FREECAD ASSEMBLY — COMPONENT RECIPES ("1.1deltabot_assembly")

This assembly document has 19 components, labeled P0..P18 below (a component is one placed body or linked part). 10 of them carry a construction recipe — the FreeCAD feature program that regenerates the part from scratch, quoted from this document or its linked companion documents; the rest are supplied as boundary geometry only. No exploded tour is included for this assembly.
COMPONENT P0 — geometry summary ("motorb"; no construction recipe available for this part):
  bounding box: 75.4 x 57.0 x 56.7 mm
  tessellated surface: 25,604 triangles
  volume: 98013 mm^3 (40% of its bounding box)
COMPONENT P1 — geometry summary ("motorc"; no construction recipe available for this part):
  bounding box: 79.7 x 76.4 x 56.8 mm
  tessellated surface: 25,604 triangles
  volume: 98013 mm^3 (28% of its bounding box)
COMPONENT P2 — geometry summary ("SI8T/K Rod End Bearing v003"; no construction recipe available for this part):
  bounding box: 49.0 x 32.7 x 24.1 mm
  tessellated surface: 22,464 triangles
  volume: 6438 mm^3 (17% of its bounding box)
COMPONENT P3 — geometry summary ("SI8T/K Rod End Bearing v004"; no construction recipe available for this part):
  bounding box: 45.7 x 35.5 x 30.6 mm
  tessellated surface: 22,464 triangles
  volume: 6438 mm^3 (13% of its bounding box)
COMPONENT P4 — geometry summary ("SI8T/K Rod End Bearing v005"; no construction recipe available for this part):
  bounding box: 45.7 x 35.5 x 30.6 mm
  tessellated surface: 22,464 triangles
  volume: 6438 mm^3 (13% of its bounding box)
COMPONENT P5 — geometry summary ("SI8T/K Rod End Bearing v006"; no construction recipe available for this part):
  bounding box: 48.3 x 35.5 x 14.1 mm
  tessellated surface: 22,464 triangles
  volume: 6438 mm^3 (27% of its bounding box)
COMPONENT P6 — geometry summary ("SI8T/K Rod End Bearing v007"; no construction recipe available for this part):
  bounding box: 48.3 x 35.5 x 14.1 mm
  tessellated surface: 22,464 triangles
  volume: 6438 mm^3 (27% of its bounding box)
COMPONENT P7 — geometry summary ("SI8T/K Rod End Bearing v2"; no construction recipe available for this part):
  bounding box: 49.0 x 32.7 x 24.1 mm
  tessellated surface: 22,464 triangles
  volume: 6438 mm^3 (17% of its bounding box)
COMPONENT P8 — recipe-attached ("base", a linked part whose construction recipe lives in a companion FreeCAD document of the same project; that document's serialized recipe follows).
Construction recipe (the companion document, serialized — sketch geometry with constraints, then the solid features built on it; lengths are millimeters unless a unit is written):

FCSTD DOCUMENT  (FreeCAD 1.0R38641 +468 (Git))
Label: main
License: All rights reserved
LicenseURL: https://en.wikipedia.org/wiki/All_rights_reserved
objects: Sketcher::SketchObject×17, PartDesign::Pad×10, PartDesign::Body×7, PartDesign::Plane×6, PartDesign::Pocket×4, App::Part×4, PartDesign::ShapeBinder×2, PartDesign::Chamfer×2, Spreadsheet::Sheet×1, PartDesign::AdditiveLoft×1, PartDesign::Fillet×1, PartDesign::SubtractiveBox×1, PartDesign::PolarPattern×1
note: 108 computed .brp shape members not serialized (recipe doc carries the construction recipe); baked Part::Feature solids carry a one-line shape summary decoded from their .brp

FEATURE [Spreadsheet::Sheet] Spreadsheet  label="ss"
  cells = A1='deltabot calculation - values for kinetic | https://www.marginallyclever.com/other/samples/fk-ik-test.html; A3='Base radius (f); B3(f)=300; D3='vslot_length; E3(vslot_length)==<<main>>#<<base_triangle_sketch>>.Constraints.vslot_length; A4='Bicep length (rf); B4(rf)=200; C4='!= tube actual length; A5='Bicep inerdia (od_rf); B5(od_rf)=30; A6='Bicep outerdia (id_rf); B6(id_rf)=27.95; A7='Bicep end length (end_rf); B7(end_rf)=25; A11='Forearm length (re); B11(re)=300; A12='End Effector radius (e); A13='Base to floor distance (b)
FEATURE [Sketcher::SketchObject] Sketch
  ArcFitTolerance = 0
  AttachmentSupport = -> [XY_Plane]
  FullyConstrained = true
  MakeInternals = false
  MapMode = 5
  sketch-geometry (1):
    g0: Circle CenterX=0 CenterY=0 CenterZ=0 NormalX=0 NormalY=0 NormalZ=1 AngleXU=0 Radius=4
  constraints (2):
    c: Coincident(g0,g-1)
    c: Diameter(g0) = 8
FEATURE [PartDesign::Pad] Pad
  Direction = (0,0,1)
  Length = 300
  Length2 = 10
  Midplane = true
  Profile = -> Sketch
  ReferenceAxis = -> Sketch [N_Axis]
  Suppressed = false
  Type = 0
  expr: Length = Spreadsheet.re
FEATURE [Sketcher::SketchObject] Sketch001
  ArcFitTolerance = 0
  AttachmentSupport = -> [XY_Plane001]
  FullyConstrained = true
  MakeInternals = false
  MapMode = 5
  expr: Constraints[1] = Spreadsheet.od_rf
  expr: Constraints[3] = <<ss>>.id_rf
  sketch-geometry (2):
    g0: Circle CenterX=0 CenterY=0 CenterZ=0 NormalX=0 NormalY=0 NormalZ=1 AngleXU=0 Radius=15
    g1: Circle CenterX=0 CenterY=0 CenterZ=0 NormalX=0 NormalY=0 NormalZ=1 AngleXU=0 Radius=13.975
  constraints (4):
    c: Coincident(g0,g-1)
    c: Diameter(g0) = 30
    c: Coincident(g1,g0)
    c: Diameter(g1) = 27.95
FEATURE [PartDesign::Pad] Pad001
  Direction = (0,0,1)
  Length = 146
  Length2 = 10
  Midplane = true
  Profile = -> Sketch001
  ReferenceAxis = -> Sketch001 [N_Axis]
  Suppressed = false
  Type = 0
  expr: Length = <<ss>>.rf - <<ss>>.end_rf - 29
FEATURE [PartDesign::Body] Body001  label="tube_bicep"
  AllowCompound = false
  Group = -> [Sketch001,Pad001]
  Origin = -> Origin001
  Tip = -> Pad001
FEATURE [PartDesign::ShapeBinder] ReferencePad001
  Placement = pos=(0,0,73) rot=(0,0,1;0rad)
  Support = -> [Pad001]
  TraceSupport = false
FEATURE [PartDesign::Plane] DatumPlane
  AttachmentSupport = -> [ReferencePad001]
  Length = 61.3058
  MapMode = 5
  Placement = pos=(0,0,73) rot=(0,0,1;0rad)
  ResizeMode = 0
  Width = 75.2168
FEATURE [Sketcher::SketchObject] Sketch002
  ArcFitTolerance = 0
  AttachmentSupport = -> [DatumPlane]
  FullyConstrained = true
  MakeInternals = false
  MapMode = 5
  Placement = pos=(0,0,73) rot=(0,0,1;0rad)
  expr: Constraints[1] = <<ss>>.id_rf
  sketch-geometry (1):
    g0: Circle CenterX=0 CenterY=0 CenterZ=0 NormalX=0 NormalY=0 NormalZ=1 AngleXU=0 Radius=13.975
  constraints (2):
    c: Coincident(g0,g-1)
    c: Diameter(g0) = 27.95
FEATURE [PartDesign::Pad] Pad002
  Direction = (0,0,1)
  Length = 15
  Length2 = 10
  Placement = pos=(0,0,73) rot=(0,0,1;0rad)
  Profile = -> Sketch002
  ReferenceAxis = -> Sketch002 [N_Axis]
  Reversed = true
  Suppressed = false
  Type = 0
FEATURE [Sketcher::SketchObject] Sketch003
  ArcFitTolerance = 0
  AttachmentSupport = -> [DatumPlane]
  FullyConstrained = true
  MakeInternals = false
  MapMode = 5
  Placement = pos=(0,0,73) rot=(0,0,1;0rad)
  expr: Constraints[1] = <<ss>>.od_rf
  sketch-geometry (1):
    g0: Circle CenterX=0 CenterY=0 CenterZ=0 NormalX=0 NormalY=0 NormalZ=1 AngleXU=0 Radius=15
  constraints (2):
    c: Coincident(g0,g-1)
    c: Diameter(g0) = 30
FEATURE [PartDesign::Pad] Pad003
  BaseFeature = -> Pad002
  Direction = (0,0,1)
  Length = 25
  Length2 = 10
  Placement = pos=(0,0,73) rot=(0,0,1;0rad)
  Profile = -> Sketch003
  ReferenceAxis = -> Sketch003 [N_Axis]
  Suppressed = false
  Type = 0
  expr: Length = <<ss>>.end_rf
FEATURE [PartDesign::Plane] DatumPlane001
  AttachmentOffset = pos=(0,0,0) rot=(0,1,0;1.5708rad)
  AttachmentSupport = -> [Pad003]
  Length = 138.272
  MapMode = 45
  Placement = pos=(-1.8e-15,1e-16,85.5) rot=(0,1,0;1.5708rad)
  ResizeMode = 0
  Width = 81.4772
FEATURE [Sketcher::SketchObject] Sketch004
  ArcFitTolerance = 0
  AttachmentSupport = -> [DatumPlane001]
  ExternalGeometry = -> [Pad003]
  FullyConstrained = false
  MakeInternals = false
  MapMode = 5
  Placement = pos=(-1.8e-15,1e-16,85.5) rot=(0,1,0;1.5708rad)
  sketch-geometry (6):
    g0: Circle CenterX=0 CenterY=-22.7402 CenterZ=0 NormalX=0 NormalY=0 NormalZ=1 AngleXU=0 Radius=3
    g1: ArcOfCircle CenterX=0 CenterY=-22.7402 CenterZ=0 NormalX=0 NormalY=0 NormalZ=1 AngleXU=0 Radius=7.5 StartAngle=2.63197 EndAngle=6.07379
    g2: LineSegment StartX=-6.54695 StartY=-19.0813 StartZ=0 EndX=4.11697 EndY=0 EndZ=0
    g3: LineSegment StartX=4.11697 StartY=0 StartZ=0 EndX=12.5 EndY=0 EndZ=0
    g4: LineSegment StartX=7.33618 StartY=-24.2992 StartZ=0 EndX=12.5 EndY=0 EndZ=0
    g5: LineSegment [constr] StartX=12.5 StartY=15 StartZ=0 EndX=-6.54695 EndY=-19.0813 EndZ=0
  constraints (14):
    c: PointOnObject(g0,g-2)
    c: Diameter(g0) = 6
    c: Coincident(g1,g0)
    c: Diameter(g1) = 15
    c: Tangent(g1,g2) = 1.5708
    c: Coincident(g2,g3)
    c: Horizontal(g3)
    c: PointOnObject(g2,g-1)
    c: Tangent(g1,g4) = -1.5708
    c: Coincident(g4,g3)
    c: PointOnObject(g3,g-5)
    c: Coincident(g5,g-4)
    c: Coincident(g5,g1)
    c: PointOnObject(g2,g5)
FEATURE [PartDesign::Pad] Pad004
  BaseFeature = -> Pad003
  Direction = (1,0,2e-16)
  Length = 30
  Length2 = 10
  Midplane = true
  Placement = pos=(0,0,73) rot=(0,0,1;0rad)
  Profile = -> Sketch004
  ReferenceAxis = -> Sketch004 [N_Axis]
  Suppressed = false
  Type = 0
  expr: Length = <<ss>>.od_rf
FEATURE [PartDesign::ShapeBinder] ReferencePad002
  Placement = pos=(0,0,-73) rot=(0,0,1;0rad)
  Support = -> [Pad001]
  TraceSupport = false
FEATURE [PartDesign::Plane] DatumPlane002
  AttachmentSupport = -> [ReferencePad002]
  Length = 60
  MapMode = 5
  Placement = pos=(0,0,-73) rot=(1,0,0;3.14159rad)
  ResizeMode = 0
  Width = 60
FEATURE [Sketcher::SketchObject] Sketch005
  ArcFitTolerance = 0
  AttachmentSupport = -> [DatumPlane002]
  FullyConstrained = true
  MakeInternals = false
  MapMode = 5
  Placement = pos=(0,0,-73) rot=(1,0,0;3.14159rad)
  expr: Constraints[1] = <<ss>>.id_rf
  sketch-geometry (1):
    g0: Circle CenterX=0 CenterY=0 CenterZ=0 NormalX=0 NormalY=0 NormalZ=1 AngleXU=0 Radius=13.975
  constraints (2):
    c: Coincident(g0,g-1)
    c: Diameter(g0) = 27.95
FEATURE [PartDesign::Pad] Pad005
  Direction = (0,0,-1)
  Length = 15
  Length2 = 10
  Placement = pos=(0,0,-73) rot=(1,0,0;3.14159rad)
  Profile = -> Sketch005
  ReferenceAxis = -> Sketch005 [N_Axis]
  Reversed = true
  Suppressed = false
  Type = 0
FEATURE [Sketcher::SketchObject] Sketch006
  ArcFitTolerance = 0
  AttachmentSupport = -> [DatumPlane002]
  FullyConstrained = true
  MakeInternals = false
  MapMode = 5
  Placement = pos=(0,0,-73) rot=(1,0,0;3.14159rad)
  expr: Constraints[1] = <<ss>>.od_rf
  sketch-geometry (1):
    g0: Circle CenterX=0 CenterY=0 CenterZ=0 NormalX=0 NormalY=0 NormalZ=1 AngleXU=0 Radius=15
  constraints (2):
    c: Coincident(g0,g-1)
    c: Diameter(g0) = 30
FEATURE [PartDesign::Plane] DatumPlane003
  AttachmentOffset = pos=(0,0,20) rot=(0,0,1;0rad)
  AttachmentSupport = -> [DatumPlane002]
  Length = 60
  MapMode = 5
  Placement = pos=(0,0,-93) rot=(1,0,0;3.14159rad)
  ResizeMode = 0
  Width = 60
FEATURE [Sketcher::SketchObject] Sketch007
  ArcFitTolerance = 0
  AttachmentSupport = -> [DatumPlane003]
  FullyConstrained = true
  MakeInternals = false
  MapMode = 5
  Placement = pos=(0,0,-93) rot=(1,0,0;3.14159rad)
  expr: Constraints[10] = <<ss>>.od_rf
  expr: Constraints[11] = <<ss>>.od_rf
  sketch-geometry (5):
    g0: LineSegment StartX=-15 StartY=-15 StartZ=0 EndX=-15 EndY=15 EndZ=0
    g1: LineSegment StartX=-15 StartY=15 StartZ=0 EndX=15 EndY=15 EndZ=0
    g2: LineSegment StartX=15 StartY=15 StartZ=0 EndX=15 EndY=-15 EndZ=0
    g3: LineSegment StartX=15 StartY=-15 StartZ=0 EndX=-15 EndY=-15 EndZ=0
    g4: GeomPoint [constr] X=0 Y=0 Z=0
  constraints (12):
    c: Coincident(g0,g1)
    c: Coincident(g1,g2)
    c: Coincident(g2,g3)
    c: Coincident(g3,g0)
    c: Horizontal(g1)
    c: Horizontal(g3)
    c: Vertical(g0)
    c: Vertical(g2)
    c: Symmetric(g1,g0,g4)
    c: Coincident(g4,g-1)
    c: DistanceX(g1,g1) = 30
    c: DistanceY(g2,g2) = 30
FEATURE [PartDesign::AdditiveLoft] AdditiveLoft
  BaseFeature = -> Pad005
  Closed = false
  Placement = pos=(0,0,-73) rot=(1,0,0;3.14159rad)
  Profile = -> Sketch006
  Ruled = false
  Sections = -> [Sketch007]
  Suppressed = false
FEATURE [PartDesign::Pad] Pad006
  BaseFeature = -> AdditiveLoft
  Direction = (0,0,-1)
  Length = 15
  Length2 = 10
  Placement = pos=(0,0,-73) rot=(1,0,0;3.14159rad)
  Profile = -> Sketch007
  ReferenceAxis = -> Sketch007 [N_Axis]
  Suppressed = false
  Type = 0
  expr: Length = <<ss>>.od_rf * 0.5
FEATURE [PartDesign::Fillet] Fillet
  Base = -> Pad006 [Edge25,Edge23]
  BaseFeature = -> Pad006
  Placement = pos=(0,0,-73) rot=(1,0,0;3.14159rad)
  Radius = 13.5
  SupportTransform = false
  Suppressed = false
  UseAllEdges = false
  expr: Radius = <<ss>>.od_rf * 0.45
FEATURE [PartDesign::Chamfer] Chamfer
  Angle = 45
  Base = -> Fillet [Face1,Face9]
  BaseFeature = -> Fillet
  ChamferType = 0
  FlipDirection = false
  Placement = pos=(0,0,-73) rot=(1,0,0;3.14159rad)
  Size = 1
  Size2 = 1
  SupportTransform = false
  Suppressed = false
  UseAllEdges = false
FEATURE [Sketcher::SketchObject] Sketch008
  ArcFitTolerance = 0
  AttachmentSupport = -> [Chamfer]
  ExternalGeometry = -> [Chamfer]
  FullyConstrained = true
  MakeInternals = false
  MapMode = 5
  Placement = pos=(15,0,-73) rot=(0.57735,-0.57735,0.57735;4.18879rad)
  expr: Constraints[7] = 7.5 / 2 - 0.1
  sketch-geometry (3):
    g0: Circle [constr] CenterX=-1.8e-15 CenterY=21 CenterZ=0 NormalX=0 NormalY=0 NormalZ=1 AngleXU=0 Radius=4.05
    g1: ArcOfCircle CenterX=-1.8e-15 CenterY=21 CenterZ=0 NormalX=0 NormalY=0 NormalZ=1 AngleXU=0 Radius=4.05 StartAngle=2.01898 EndAngle=7.4058
    g2: LineSegment StartX=-1.75499 StartY=24.65 StartZ=0 EndX=1.75499 EndY=24.65 EndZ=0
  constraints (8):
    c: Diameter(g0) = 8.1
    c: PointOnObject(g1,g0)
    c: Coincident(g1,g0)
    c: Coincident(g0,g-4)
    c: Horizontal(g2)
    c: Coincident(g1,g2)
    c: Coincident(g1,g2)
    c: DistanceY(g0,g1) = 3.65
FEATURE [PartDesign::Pocket] Pocket
  BaseFeature = -> Chamfer
  Direction = (-1,0,0)
  Length = 5
  Length2 = 5
  Placement = pos=(0,0,-73) rot=(1,0,0;3.14159rad)
  Profile = -> Sketch008
  ReferenceAxis = -> Sketch008 [N_Axis]
  Suppressed = false
  Type = 1
FEATURE [PartDesign::SubtractiveBox] Box
  AttacherType = Attacher::AttachEngine3D
  AttachmentOffset = pos=(-23,-39,0) rot=(0,0,1;0rad)
  AttachmentSupport = -> [Pad004]
  BaseFeature = -> Pad004
  Height = 44
  Length = 44
  MapMode = 5
  Placement = pos=(-23,-30.4742,98.4141) rot=(-1,0,0;0.509626rad)
  Refine = true
  Suppressed = false
  Width = 61
FEATURE [App::Part] Part002  label="tool"
  Origin = -> Origin010
FEATURE [Sketcher::SketchObject] Sketch010
  ArcFitTolerance = 1e-06
  AttachmentSupport = -> [XY_Plane011]
  FullyConstrained = true
  MakeInternals = false
  MapMode = 5
FEATURE [PartDesign::Body] Body  label="forearm_axis"
  AllowCompound = false
  Group = -> [Sketch,Pad,Sketch010]
  Origin = -> Origin
  Tip = -> Pad
FEATURE [App::Part] Part001  label="forearm"
  Group = -> [Body]
  Origin = -> Origin009
FEATURE [Sketcher::SketchObject] Sketch011  label="base_triangle_sketch"
  ArcFitTolerance = 1e-06
  AttachmentSupport = -> [XY_Plane012]
  FullyConstrained = true
  MakeInternals = false
  MapMode = 5
  sketch-geometry (12):
    g0: Circle [constr] CenterX=0 CenterY=0 CenterZ=0 NormalX=0 NormalY=0 NormalZ=1 AngleXU=0 Radius=150
    g1: LineSegment StartX=0 StartY=35 StartZ=0 EndX=-30.3109 EndY=-17.5 EndZ=0
    g2: LineSegment StartX=-30.3109 StartY=-17.5 StartZ=0 EndX=30.3109 EndY=-17.5 EndZ=0
    g3: LineSegment StartX=30.3109 StartY=-17.5 StartZ=0 EndX=0 EndY=35 EndZ=0
    g4: Circle [constr] CenterX=0 CenterY=0 CenterZ=0 NormalX=0 NormalY=0 NormalZ=1 AngleXU=0 Radius=35
    g5: LineSegment StartX=0 StartY=75 StartZ=0 EndX=-64.9519 EndY=-37.5 EndZ=0
    g6: LineSegment StartX=-64.9519 StartY=-37.5 StartZ=0 EndX=64.9519 EndY=-37.5 EndZ=0
    g7: LineSegment StartX=64.9519 StartY=-37.5 StartZ=0 EndX=0 EndY=75 EndZ=0
    g8: Circle [constr] CenterX=0 CenterY=0 CenterZ=0 NormalX=0 NormalY=0 NormalZ=1 AngleXU=0 Radius=75
    g9: LineSegment [constr] StartX=0 StartY=35 StartZ=0 EndX=89.6433 EndY=-120.267 EndZ=0
    g10: LineSegment [constr] StartX=30.3109 StartY=-17.5 StartZ=0 EndX=-148.976 EndY=-17.5 EndZ=0
    g11: LineSegment [constr] StartX=-30.3109 StartY=-17.5 StartZ=0 EndX=59.3324 EndY=137.767 EndZ=0
  constraints (34):
    c: Diameter(g0) = 300
    c: Coincident(g0,g-1)
    c: Coincident(g1,g2)
    c: Coincident(g2,g3)
    c: Coincident(g3,g1)
    c: Equal(g1,g2)
    c: Equal(g1,g3)
    c: PointOnObject(g1,g4)
    c: PointOnObject(g2,g4)
    c: PointOnObject(g3,g4)
    c: Coincident(g4,g0)
    c: Coincident(g5,g6)
    c: Coincident(g6,g7)
    c: Coincident(g7,g5)
    c: Equal(g5,g6)
    c: Equal(g5,g7)
    c: PointOnObject(g5,g8)
    c: PointOnObject(g6,g8)
    c: PointOnObject(g7,g8)
    c: Coincident(g8,g0)
    c: PointOnObject(g1,g-2)
    c: PointOnObject(g5,g-2)
    c: Distance(g7,g3) = 20
    c: Coincident(g9,g1)
    c: PointOnObject(g9,g0)
    c: PointOnObject(g2,g9)
    c: Coincident(g10,g2)
    c: PointOnObject(g10,g0)
    c: Horizontal(g10)
    c: Coincident(g11,g1)
    c: PointOnObject(g3,g11)
    c: PointOnObject(g11,g0)
    c: Diameter(g8) = 150
    c: Distance(g9,g9) = 179.287  'vslot_length'
FEATURE [PartDesign::Pad] Pad007
  Direction = (0,0,1)
  Length = 10
  Length2 = 10
  Profile = -> Sketch011
  ReferenceAxis = -> Sketch011 [N_Axis]
  Refine = true
  Suppressed = false
  Type = 0
FEATURE [Sketcher::SketchObject] Sketch015
  ArcFitTolerance = 1e-06
  AttachmentSupport = -> [XY_Plane014]
  FullyConstrained = false
  MakeInternals = false
  MapMode = 5
  sketch-geometry (50):
    g0: ArcOfCircle CenterX=0 CenterY=0 CenterZ=0 NormalX=0 NormalY=0 NormalZ=1 AngleXU=0 Radius=2.5 StartAngle=3.14159 EndAngle=6.28319
    g1: LineSegment StartX=-10 StartY=-5.1 StartZ=0 EndX=-10 EndY=-8.5 EndZ=0
    g2: ArcOfCircle CenterX=-8.5 CenterY=-8.5 CenterZ=0 NormalX=0 NormalY=0 NormalZ=1 AngleXU=0 Radius=1.5 StartAngle=3.14159 EndAngle=4.71239
    g3: LineSegment StartX=-8.5 StartY=-10 StartZ=0 EndX=-5.1 EndY=-10 EndZ=0
    g4: LineSegment StartX=-5.1 StartY=-10 StartZ=0 EndX=-3.1 EndY=-8 EndZ=0
    g5: LineSegment StartX=-3.1 StartY=-8 StartZ=0 EndX=-5.3 EndY=-8 EndZ=0
    g6: LineSegment StartX=-5.3 StartY=-8 StartZ=0 EndX=-5.3 EndY=-6.57279 EndZ=0
    g7: LineSegment StartX=-5.3 StartY=-6.57279 StartZ=0 EndX=-2.72721 EndY=-4 EndZ=0
    g8: LineSegment StartX=-2.72721 StartY=-4 StartZ=0 EndX=2.72721 EndY=-4 EndZ=0
    g9: LineSegment StartX=2.72721 StartY=-4 StartZ=0 EndX=5.3 EndY=-6.57279 EndZ=0
    g10: LineSegment StartX=5.3 StartY=-6.57279 StartZ=0 EndX=5.3 EndY=-8 EndZ=0
    g11: LineSegment StartX=5.3 StartY=-8 StartZ=0 EndX=3.1 EndY=-8 EndZ=0
    g12: LineSegment StartX=3.1 StartY=-8 StartZ=0 EndX=5.1 EndY=-10 EndZ=0
    g13: LineSegment StartX=5.1 StartY=-10 StartZ=0 EndX=8.5 EndY=-10 EndZ=0
    g14: ArcOfCircle CenterX=8.5 CenterY=-8.5 CenterZ=0 NormalX=0 NormalY=0 NormalZ=1 AngleXU=0 Radius=1.5 StartAngle=4.71239 EndAngle=6.28319
    g15: LineSegment StartX=10 StartY=-8.5 StartZ=0 EndX=10 EndY=-5.1 EndZ=0
    g16: LineSegment StartX=10 StartY=-5.1 StartZ=0 EndX=8 EndY=-3.1 EndZ=0
    g17: LineSegment StartX=8 StartY=-3.1 StartZ=0 EndX=8 EndY=-5.3 EndZ=0
    g18: LineSegment StartX=8 StartY=-5.3 StartZ=0 EndX=6.57279 EndY=-5.3 EndZ=0
    g19: LineSegment StartX=6.57279 StartY=-5.3 StartZ=0 EndX=4 EndY=-2.72721 EndZ=0
    g20: LineSegment StartX=4 StartY=-2.72721 StartZ=0 EndX=4 EndY=2.72721 EndZ=0
    g21: LineSegment StartX=4 StartY=2.72721 StartZ=0 EndX=6.57279 EndY=5.3 EndZ=0
    g22: LineSegment StartX=6.57279 StartY=5.3 StartZ=0 EndX=8 EndY=5.3 EndZ=0
    g23: LineSegment StartX=8 StartY=5.3 StartZ=0 EndX=8 EndY=3.1 EndZ=0
    g24: LineSegment StartX=8 StartY=3.1 StartZ=0 EndX=10 EndY=5.1 EndZ=0
    g25: LineSegment StartX=10 StartY=5.1 StartZ=0 EndX=10 EndY=8.5 EndZ=0
    g26: ArcOfCircle CenterX=8.5 CenterY=8.5 CenterZ=0 NormalX=0 NormalY=0 NormalZ=1 AngleXU=0 Radius=1.5 StartAngle=0 EndAngle=1.5708
    g27: LineSegment StartX=8.5 StartY=10 StartZ=0 EndX=5.1 EndY=10 EndZ=0
    g28: LineSegment StartX=5.1 StartY=10 StartZ=0 EndX=3.1 EndY=8 EndZ=0
    g29: LineSegment StartX=3.1 StartY=8 StartZ=0 EndX=5.3 EndY=8 EndZ=0
    g30: LineSegment StartX=5.3 StartY=8 StartZ=0 EndX=5.3 EndY=6.57279 EndZ=0
    g31: LineSegment StartX=5.3 StartY=6.57279 StartZ=0 EndX=2.72721 EndY=4 EndZ=0
    g32: LineSegment StartX=2.72721 StartY=4 StartZ=0 EndX=-2.72721 EndY=4 EndZ=0
    g33: LineSegment StartX=-2.72721 StartY=4 StartZ=0 EndX=-5.3 EndY=6.57279 EndZ=0
    g34: LineSegment StartX=-5.3 StartY=6.57279 StartZ=0 EndX=-5.3 EndY=8 EndZ=0
    g35: LineSegment StartX=-5.3 StartY=8 StartZ=0 EndX=-3.1 EndY=8 EndZ=0
    g36: LineSegment StartX=-3.1 StartY=8 StartZ=0 EndX=-5.1 EndY=10 EndZ=0
    g37: LineSegment StartX=-5.1 StartY=10 StartZ=0 EndX=-8.5 EndY=10 EndZ=0
    g38: ArcOfCircle CenterX=-8.5 CenterY=8.5 CenterZ=0 NormalX=0 NormalY=0 NormalZ=1 AngleXU=0 Radius=1.5 StartAngle=1.5708 EndAngle=3.14159
    g39: LineSegment StartX=-10 StartY=8.5 StartZ=0 EndX=-10 EndY=5.1 EndZ=0
    g40: LineSegment StartX=-10 StartY=5.1 StartZ=0 EndX=-8 EndY=3.1 EndZ=0
    g41: LineSegment StartX=-8 StartY=3.1 StartZ=0 EndX=-8 EndY=5.3 EndZ=0
    g42: LineSegment StartX=-8 StartY=5.3 StartZ=0 EndX=-6.57279 EndY=5.3 EndZ=0
    g43: LineSegment StartX=-6.57279 StartY=5.3 StartZ=0 EndX=-4 EndY=2.72721 EndZ=0
    g44: LineSegment StartX=-4 StartY=2.72721 StartZ=0 EndX=-4 EndY=-2.72721 EndZ=0
    g45: LineSegment StartX=-4 StartY=-2.72721 StartZ=0 EndX=-6.57279 EndY=-5.3 EndZ=0
    g46: LineSegment StartX=-6.57279 StartY=-5.3 StartZ=0 EndX=-8 EndY=-5.3 EndZ=0
    g47: LineSegment StartX=-8 StartY=-5.3 StartZ=0 EndX=-8 EndY=-3.1 EndZ=0
    g48: LineSegment StartX=-8 StartY=-3.1 StartZ=0 EndX=-10 EndY=-5.1 EndZ=0
    g49: ArcOfCircle CenterX=0 CenterY=0 CenterZ=0 NormalX=0 NormalY=0 NormalZ=1 AngleXU=0 Radius=2.5 StartAngle=0 EndAngle=3.14159
FEATURE [Sketcher::SketchObject] Sketch012
  ArcFitTolerance = 1e-06
  AttachmentSupport = -> [XY_Plane012]
  ExternalGeometry = -> [Sketch011]
  FullyConstrained = true
  MakeInternals = false
  MapMode = 5
  sketch-geometry (4):
    g0: Circle CenterX=11.3157 CenterY=35.4006 CenterZ=0 NormalX=0 NormalY=0 NormalZ=1 AngleXU=0 Radius=2.5
    g1: LineSegment [constr] StartX=-30.3109 StartY=-17.5 StartZ=0 EndX=32.476 EndY=18.75 EndZ=0
    g2: LineSegment [constr] StartX=23.8157 StartY=13.75 StartZ=0 EndX=11.3157 EndY=35.4006 EndZ=0
    g3: Circle CenterX=36.3157 CenterY=-7.90064 CenterZ=0 NormalX=0 NormalY=0 NormalZ=1 AngleXU=0 Radius=2.5
  constraints (11):
    c: Perpendicular(g-3,g1)
    c: Coincident(g1,g-4)
    c: PointOnObject(g2,g1)
    c: Perpendicular(g1,g2)
    c: PointOnObject(g1,g-3)
    c: Distance(g2,g1) = 10
    c: Coincident(g0,g2)
    c: Symmetric(g0,g3,g2)
    c: Equal(g3,g0)
    c: Diameter(g0) = 5
    c: Distance(g0,g3) = 50
FEATURE [PartDesign::Pocket] Pocket003
  BaseFeature = -> Pad007
  Direction = (0,0,-1)
  Length = 5
  Length2 = 5
  Profile = -> Sketch012
  ReferenceAxis = -> Sketch012 [N_Axis]
  Refine = true
  Reversed = true
  Suppressed = false
  Type = 1
FEATURE [PartDesign::PolarPattern] PolarPattern
  Angle = 360
  Axis = -> Sketch012 [N_Axis]
  BaseFeature = -> Pocket003
  Mode = 0
  Occurrences = 3
  Offset = 120
  Originals = -> [Pocket003]
  Refine = true
  Suppressed = false
  TransformMode = 0
FEATURE [PartDesign::Body] Body004  label="base_triangle"
  AllowCompound = false
  Group = -> [Sketch011,Pad007,Sketch012,Pocket003,PolarPattern]
  Origin = -> Origin012
  Tip = -> PolarPattern
FEATURE [App::Part] Part003  label="base"
  Group = -> [Body004]
  Origin = -> Origin011
FEATURE [PartDesign::Pad] Pad008
  Direction = (0,0,1)
  Length = 179.287
  Length2 = 10
  Profile = -> Sketch015
  ReferenceAxis = -> Sketch015 [N_Axis]
  Refine = true
  Suppressed = false
  Type = 0
  expr: Length = <<ss>>.vslot_length
FEATURE [PartDesign::Body] Body006  label="vslot"
  AllowCompound = false
  Group = -> [Sketch015,Pad008]
  Origin = -> Origin024
  Tip = -> Pad008
FEATURE [Sketcher::SketchObject] Sketch016
  ArcFitTolerance = 1e-06
  AttachmentSupport = -> [XY_Plane015]
  FullyConstrained = false
  MakeInternals = false
  MapMode = 5
  sketch-geometry (19):
    g0: Circle CenterX=0 CenterY=0 CenterZ=0 NormalX=0 NormalY=0 NormalZ=1 AngleXU=0 Radius=20
    g1: LineSegment [constr] StartX=-23.5 StartY=-23.5 StartZ=0 EndX=23.5 EndY=-23.5 EndZ=0
    g2: LineSegment [constr] StartX=23.5 StartY=-23.5 StartZ=0 EndX=23.5 EndY=23.5 EndZ=0
    g3: LineSegment [constr] StartX=23.5 StartY=23.5 StartZ=0 EndX=-23.5 EndY=23.5 EndZ=0
    g4: LineSegment [constr] StartX=-23.5 StartY=23.5 StartZ=0 EndX=-23.5 EndY=-23.5 EndZ=0
    g5: GeomPoint [constr] X=0 Y=0 Z=0
    g6: Circle CenterX=-23.5 CenterY=23.5 CenterZ=0 NormalX=0 NormalY=0 NormalZ=1 AngleXU=0 Radius=2.5
    g7: Circle CenterX=23.5 CenterY=23.5 CenterZ=0 NormalX=0 NormalY=0 NormalZ=1 AngleXU=0 Radius=2.5
    g8: Circle CenterX=23.5 CenterY=-23.5 CenterZ=0 NormalX=0 NormalY=0 NormalZ=1 AngleXU=0 Radius=2.5
    g9: Circle CenterX=-23.5 CenterY=-23.5 CenterZ=0 NormalX=0 NormalY=0 NormalZ=1 AngleXU=0 Radius=2.5
    g10: LineSegment StartX=-32.1207 StartY=46 StartZ=0 EndX=-32.1207 EndY=-33.5 EndZ=0
    g11: LineSegment StartX=-32.1207 StartY=-33.5 StartZ=0 EndX=32.1207 EndY=-33.5 EndZ=0
    g12: LineSegment StartX=32.1207 StartY=-33.5 StartZ=0 EndX=32.1207 EndY=46 EndZ=0
    g13: LineSegment StartX=32.1207 StartY=46 StartZ=0 EndX=-32.1207 EndY=46 EndZ=0
    g14: GeomPoint [constr] X=0 Y=6.25 Z=0
    g15: LineSegment [constr] StartX=-27.7523 StartY=38.4474 StartZ=0 EndX=27.7523 EndY=38.4474 EndZ=0
    g16: Circle CenterX=-27.7523 CenterY=38.4474 CenterZ=0 NormalX=0 NormalY=0 NormalZ=1 AngleXU=0 Radius=2.5
    g17: Circle CenterX=0 CenterY=38.4474 CenterZ=0 NormalX=0 NormalY=0 NormalZ=1 AngleXU=0 Radius=2.5
    g18: Circle CenterX=27.7523 CenterY=38.4474 CenterZ=0 NormalX=0 NormalY=0 NormalZ=1 AngleXU=0 Radius=2.5
  constraints (39):
    c: Coincident(g0,g-1)
    c: Coincident(g1,g2)
    c: Coincident(g2,g3)
    c: Coincident(g3,g4)
    c: Coincident(g4,g1)
    c: Horizontal(g1)
    c: Horizontal(g3)
    c: Vertical(g2)
    c: Vertical(g4)
    c: Symmetric(g3,g1,g5)
    c: Coincident(g5,g0)
    c: Coincident(g7,g2)
    c: Coincident(g8,g1)
    c: Coincident(g9,g1)
    c: Coincident(g3,g6)
    c: Equal(g1,g2)
    c: Equal(g8,g9)
    c: Equal(g9,g6)
    c: Equal(g6,g7)
    c: Coincident(g10,g11)
    c: Coincident(g11,g12)
    c: Coincident(g12,g13)
    c: Coincident(g13,g10)
    c: Vertical(g10)
    c: Vertical(g12)
    c: Horizontal(g11)
    c: Horizontal(g13)
    c: Symmetric(g12,g10,g14)
    c: PointOnObject(g14,g-2)
    c: DistanceY(g10,g1) = 10
    c: DistanceX(g3,g3) = 47
    c: Diameter(g0) = 40
    c: DistanceY(g2,g12) = 22.5
    c: Diameter(g7) = 5
    c: Symmetric(g15,g15,g-2)
    c: Diameter(g16) = 5
    c: Coincident(g16,g15)
    c: Diameter(g17) = 5
    c: Diameter(g18) = 5
FEATURE [PartDesign::Pad] Pad009
  Direction = (0,0,1)
  Length = 5
  Length2 = 10
  Profile = -> Sketch016
  ReferenceAxis = -> Sketch016 [N_Axis]
  Refine = true
  Suppressed = false
  Type = 0
FEATURE [PartDesign::Chamfer] Chamfer001
  Angle = 45
  Base = -> Pad009 [Edge2,Edge5]
  BaseFeature = -> Pad009
  ChamferType = 0
  FlipDirection = false
  Refine = true
  Size = 5
  Size2 = 1
  SupportTransform = false
  Suppressed = false
  UseAllEdges = false
FEATURE [PartDesign::Body] Body007  label="nema23_holder"
  AllowCompound = false
  Group = -> [Sketch016,Pad009,Chamfer001]
  Origin = -> Origin026
  Tip = -> Chamfer001
FEATURE [PartDesign::Plane] DatumPlane004
  AttachmentSupport = -> [Pocket]
  Length = 60
  MapMode = 5
  Placement = pos=(0,0,-108) rot=(1,0,0;3.14159rad)
  ResizeMode = 0
  Width = 60
FEATURE [Sketcher::SketchObject] Sketch017
  ArcFitTolerance = 1e-06
  AttachmentSupport = -> [DatumPlane004]
  ExternalGeometry = -> [Pocket]
  FullyConstrained = true
  MakeInternals = false
  MapMode = 5
  Placement = pos=(0,0,-108) rot=(1,0,0;3.14159rad)
  sketch-geometry (2):
    g0: Circle CenterX=10.5 CenterY=0 CenterZ=0 NormalX=0 NormalY=0 NormalZ=1 AngleXU=0 Radius=2.25
    g1: Circle CenterX=0 CenterY=0 CenterZ=0 NormalX=0 NormalY=0 NormalZ=1 AngleXU=0 Radius=2.25
  constraints (5):
    c: PointOnObject(g0,g-1)
    c: Equal(g1,g0)
    c: Diameter(g0) = 4.5
    c: Coincident(g1,g-1)
    c: DistanceX(g0,g-3) = 4.5
FEATURE [PartDesign::Pocket] Pocket004
  AlongSketchNormal = false
  BaseFeature = -> Pocket
  Direction = (0,0,1)
  Length = 13
  Length2 = 5
  Placement = pos=(0,0,-73) rot=(1,0,0;3.14159rad)
  Profile = -> Sketch017
  ReferenceAxis = -> Sketch017 [N_Axis]
  Refine = true
  Suppressed = false
  Type = 0
FEATURE [PartDesign::Plane] DatumPlane005
  AttachmentSupport = -> [Pocket004]
  Length = 66.3095
  MapMode = 5
  Placement = pos=(0,-15,-73) rot=(0,0.707107,-0.707107;3.14159rad)
  ResizeMode = 0
  Width = 149.31
FEATURE [Sketcher::SketchObject] Sketch018
  ArcFitTolerance = 1e-06
  AttachmentSupport = -> [DatumPlane005]
  ExternalGeometry = -> [Pocket004]
  FullyConstrained = true
  MakeInternals = false
  MapMode = 5
  Placement = pos=(0,-15,-73) rot=(0,0.707107,-0.707107;3.14159rad)
  sketch-geometry (2):
    g0: Circle CenterX=0 CenterY=21.5 CenterZ=0 NormalX=0 NormalY=0 NormalZ=1 AngleXU=0 Radius=2.25
    g1: Circle CenterX=-10.5 CenterY=21.5 CenterZ=0 NormalX=0 NormalY=0 NormalZ=1 AngleXU=0 Radius=2.25
  constraints (6):
    c: PointOnObject(g0,g-2)
    c: PointOnObject(g0,g-3)
    c: Diameter(g0) = 4.5
    c: PointOnObject(g1,g-3)
    c: Diameter(g1) = 4.5
    c: DistanceX(g-4,g1) = 4.5
FEATURE [PartDesign::Pocket] Pocket005
  BaseFeature = -> Pocket004
  Direction = (0,1,2e-16)
  Length = 12
  Length2 = 5
  Placement = pos=(0,0,-73) rot=(1,0,0;3.14159rad)
  Profile = -> Sketch018
  ReferenceAxis = -> Sketch018 [N_Axis]
  Refine = true
  Suppressed = false
  Type = 0
FEATURE [PartDesign::Body] Body003  label="motor_bicep"
  AllowCompound = false
  Group = -> [DatumPlane002,ReferencePad002,Sketch005,Pad005,Sketch006,DatumPlane003,Sketch007,AdditiveLoft,Pad006,Fillet,Chamfer,Sketch008,Pocket,DatumPlane004,Sketch017,Pocket004,DatumPlane005,Sketch018,Pocket005]
  Origin = -> Origin003
  Tip = -> Pocket005
FEATURE [Sketcher::SketchObject] Sketch019
  ArcFitTolerance = 1e-06
  AttachmentSupport = -> [YZ_Plane002]
  ExternalGeometry = -> [Box]
  FullyConstrained = true
  MakeInternals = false
  MapMode = 5
  Placement = pos=(0,0,0) rot=(0.57735,0.57735,0.57735;2.0944rad)
  constraints (1):
    c: DistanceY(g-4,g-3) = 12.5
FEATURE [PartDesign::Body] Body002  label="end_bicep"
  AllowCompound = false
  Group = -> [DatumPlane,ReferencePad001,Sketch002,Pad002,Sketch003,Pad003,DatumPlane001,Sketch004,Pad004,Box,Sketch019]
  Origin = -> Origin002
  Tip = -> Box
FEATURE [App::Part] Part  label="bicep"
  Group = -> [Body001,Body002,Body003]
  Origin = -> Origin008
COMPONENT P9 — same part as P8; its construction recipe is shown at P8.
COMPONENT P10 — same part as P8; its construction recipe is shown at P8.
COMPONENT P11 — same part as P8; its construction recipe is shown at P8.
COMPONENT P12 — same part as P8; its construction recipe is shown at P8.
COMPONENT P13 — same part as P8; its construction recipe is shown at P8.
COMPONENT P14 — same part as P8; its construction recipe is shown at P8.
COMPONENT P15 — same part as P8; its construction recipe is shown at P8.
COMPONENT P16 — same part as P8; its construction recipe is shown at P8.
COMPONENT P17 — same part as P8; its construction recipe is shown at P8.
COMPONENT P18 — geometry summary ("nema23_57byg201"; no construction recipe available for this part):
  bounding box: 86.1 x 85.2 x 71.6 mm
  tessellated surface: 25,604 triangles
  volume: 98013 mm^3 (19% of its bounding box)
PROVENANCE & LICENSES
A FreeCAD (.FCStd) document from a public repository crawl; recipes are the document's own serialized feature recipes (and, for linked parts, companion documents' recipes).
License: as declared in the source repository (recorded in the dataset sidecar).
